# Revit family: DC_Rheem_PLM_B3804HWT
name_source: partatom
category: Plumbing Fixtures
units: mm (PartAtom-declared; Revit-internal decimal feet)

## family parameters
Cut with Voids When Loaded = No
Host = Face
Part Type = Normal
Room Calculation Point = No
Round Connector Dimension = Use Radius
Shared = No

## types (4) — shared parameters
A1_ANZRS = 746 mm  [stored 2.44751 ft]
BaseHeight_ANZRS = 75 mm
BaseWidth_ANZRS = 75 mm
BoxHeight_ANZRS = 1195 mm  [stored 3.9206 ft]
ColdWaterPipeDistance_ANZRS = 567 mm
ColdWaterPipeRadius_ANZRS = 20 mm  [stored 0.0656168 ft]
Connection Height_ANZRS = 910 mm
Default Elevation = 1219 mm
EleBoxHeightFromBase_ANZRS = 450 mm
EleBoxHeight_ANZRS = 380 mm  [stored 1.24672 ft]
EleBoxWidth_ANZRS = 160 mm
Gas Pipe Radius = 15 mm  [stored 0.0492126 ft]
GasPipeDistance_ANZRS = 210 mm
GasPipeHeight_ANZRS = 600 mm
Height_ANZRS = 3165 mm
HotWaterPipeDistance_ANZRS = 235 mm
HotWaterPipeRadius_ANZRS = 20 mm  [stored 0.0656168 ft]
Length_ANZRS = 2635 mm  [stored 8.64501 ft]
Manufacturer = Raypak
Materials_ANZRS = Raypak - Stainless Steel
PVRDistance_ANZRS = 400 mm  [stored 1.31234 ft]
PVRRadius_ANZRS = 15 mm  [stored 0.0492126 ft]
TopBigDiameter_ANZRS = 1050 mm
TopH1_ANZRS = 400 mm  [stored 1.31234 ft]
TopH2_ANZRS = 750 mm
TopSmallDiameter_ANZRS = 650 mm  [stored 2.13255 ft]
URL = http://www.rheem.com.au
Width_ANZRS = 1430 mm  [stored 4.6916 ft]
zero-valued in all types: BaseDistance_ANZRS

## per-type parameters (varying)
| type | Description | Model | Type Comments |
| Raypak - Gas Water Heater- Outdoor - 3804 MJ/h  Natural gas, modulating gas control | Raypak - Gas Water Heater- Outdoor - 3804 MJ/h  Natural gas, modulating gas control | B3804NCM/HWT | Recovery 14534L/h @ 50°C rise |
| Raypak - Gas Water Heater- Outdoor - 3804 MJ/h  Natural gas, On/Off gas control | Raypak - Gas Water Heater- Outdoor - 3804 MJ/h  Natural gas, On/Off gas control | B3804NCO/HWT | Recovery 14534L/h @ 50°C rise |
| Raypak - Gas Water Heater- Outdoor - 4045 MJ/h  Propane gas, modulating gas control | Raypak - Gas Water Heater- Outdoor - 3804 MJ/h  Natural gas, modulating gas control | B3804PCM/HWT | Recovery 15409L/h @ 50°C rise |
| Raypak - Gas Water Heater- Outdoor - 4045 MJ/h  Propane gas, On/Off gas control | Raypak - Gas Water Heater- Outdoor - 4045 MJ/h  Propane gas, On/Off gas control | B3804PCO/HWT | Recovery 15409L/h @ 50°C rise |

note: [stored X ft] marks values corroborated as IEEE doubles in the binary element streams (Revit-internal decimal feet)

## geometry (parser evidence)
native form markers: Blend x4, Sweep x1
no freeform markers — native parametric forms only
